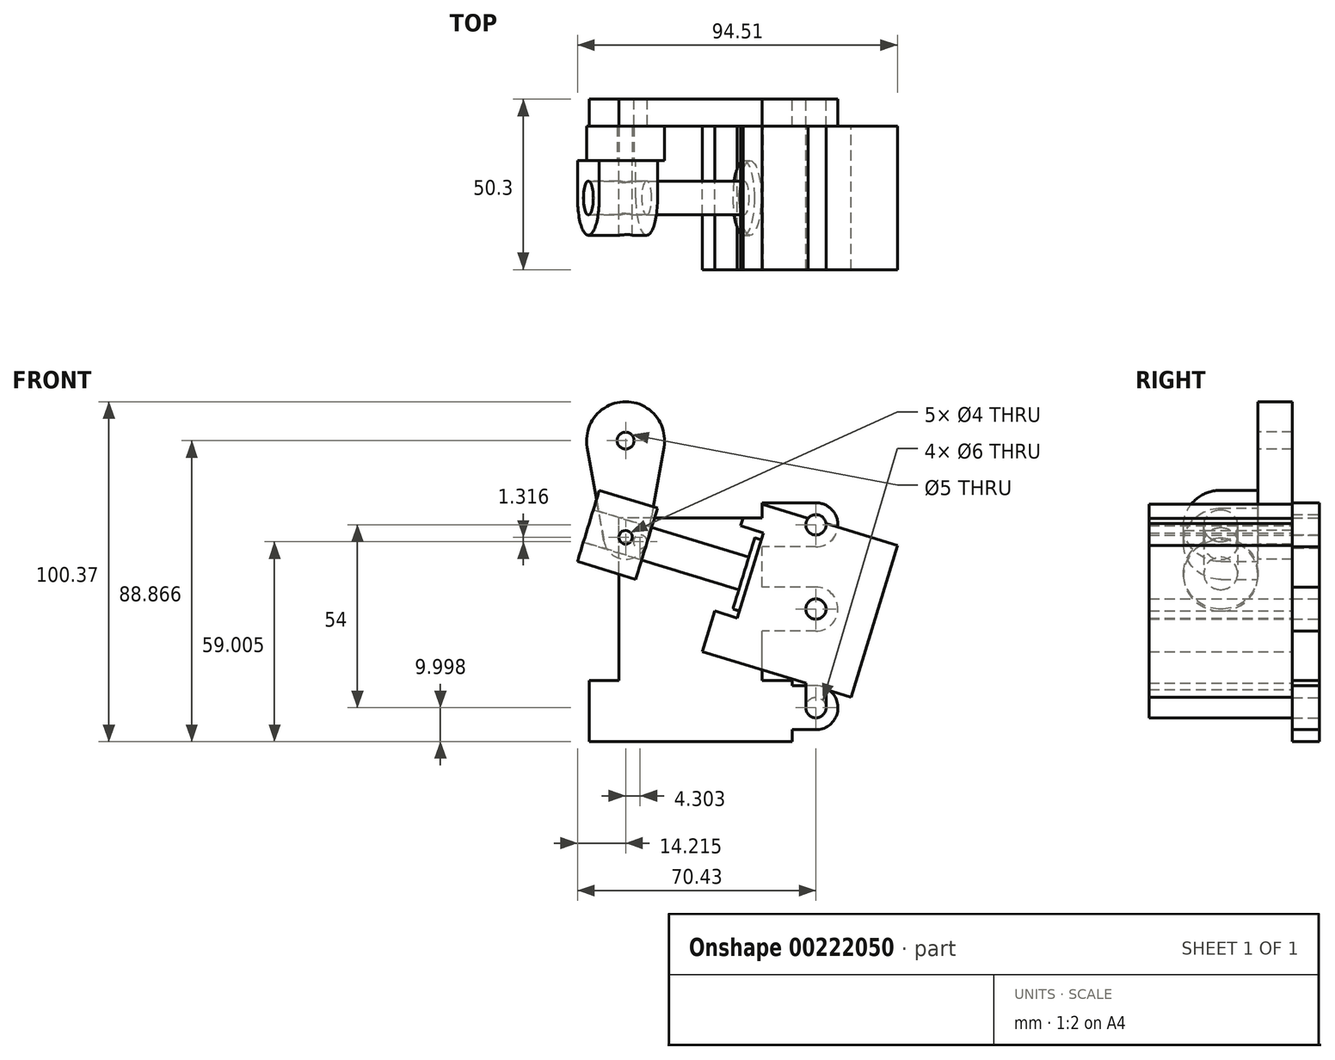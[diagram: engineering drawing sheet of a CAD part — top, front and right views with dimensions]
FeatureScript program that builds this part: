
annotation { "Feature Type Name" : "Feature", "Feature Type Description" : "" }
export const myFeature = defineFeature(function(context is Context, id is Id, definition is map)
    precondition{}
    {
        {
            var Q0;
            Q0=qCreatedBy(makeId("Front.planeOp"),FACE);
            var sketch = newSketch(context, id + "F0", { "sketchPlane" : qUnion([Q0])});
            skLineSegment(sketch, "E0.bottom", {"start": v(21.15, 20.37) * mm, "end": v(-21.15, 20.37) * mm});
            skLineSegment(sketch, "E0.top", {"start": v(21.15, 68.37) * mm, "end": v(-21.15, 68.37) * mm});
            skLineSegment(sketch, "E0.left", {"start": v(21.15, 20.37) * mm, "end": v(21.15, 68.37) * mm});
            skLineSegment(sketch, "E0.right", {"start": v(-21.15, 20.37) * mm, "end": v(-21.15, 68.37) * mm});
            skPoint(sketch, "E0.middle", {"position": v(0, 44.37) * mm});
            skLineSegment(sketch, "E1.bottom", {"start": v(-21.15, 68.37) * mm, "end": v(21.15, 68.37) * mm});
            skLineSegment(sketch, "E1.top", {"start": v(-21.15, 73.37) * mm, "end": v(21.15, 73.37) * mm});
            skLineSegment(sketch, "E1.left", {"start": v(-21.15, 68.37) * mm, "end": v(-21.15, 73.37) * mm});
            skLineSegment(sketch, "E1.right", {"start": v(21.15, 68.37) * mm, "end": v(21.15, 73.37) * mm});
            skLineSegment(sketch, "E2.bottom", {"start": v(30, 20.37) * mm, "end": v(-30, 20.37) * mm});
            skLineSegment(sketch, "E2.top", {"start": v(30, 2.37) * mm, "end": v(-30, 2.37) * mm});
            skLineSegment(sketch, "E2.left", {"start": v(30, 20.37) * mm, "end": v(30, 2.37) * mm});
            skLineSegment(sketch, "E2.right", {"start": v(-30, 20.37) * mm, "end": v(-30, 2.37) * mm});
            skPoint(sketch, "E2.middle", {"position": v(0, 11.37) * mm});
            skPoint(sketch, "E2.middle.positionSnap0", {"position": v(0, 20.37) * mm});
            skPoint(sketch, "E2.cornerSnap0", {"position": v(0, 20.37) * mm});
            skPoint(sketch, "E2.centerSnap0", {"position": v(0, 20.37) * mm});
            skCircle(sketch, "E3", {"center": v(37, 12.37) * mm, "radius": 6.5 * mm});
            skLineSegment(sketch, "E4", {"start": v(37, 5.87) * mm, "end": v(30, 5.87) * mm});
            skLineSegment(sketch, "E5", {"start": v(37, 18.87) * mm, "end": v(30, 18.87) * mm});
            skCircle(sketch, "E6", {"center": v(37, 12.37) * mm, "radius": 3 * mm});
            skCircle(sketch, "E7", {"center": v(37, 66.37) * mm, "radius": 6.5 * mm});
            skCircle(sketch, "E8", {"center": v(37, 66.37) * mm, "radius": 3 * mm});
            skLineSegment(sketch, "E9", {"start": v(37, 72.87) * mm, "end": v(21.15, 72.87) * mm});
            skLineSegment(sketch, "E10", {"start": v(37, 59.87) * mm, "end": v(21.15, 59.87) * mm});
            skCircle(sketch, "E11", {"center": v(37, 41.5) * mm, "radius": 6.5 * mm});
            skCircle(sketch, "E12", {"center": v(37, 41.5) * mm, "radius": 3 * mm});
            skLineSegment(sketch, "E13", {"start": v(37, 48) * mm, "end": v(21.15, 48) * mm});
            skLineSegment(sketch, "E14", {"start": v(37, 35) * mm, "end": v(21.15, 35) * mm});
            skSolve(sketch);
        }
        {
            var Q0;
            Q0=makeQuery(id+"F0.imprint","IMPRINT",FACE,{"disambiguationData":[TD([[makeQuery(id+"F0.imprint","IMPRINT",EDGE,{"derivedFrom":sQuery(id+"F0.wireOp",EDGE,"E1.bottom")}),1.0]])]});
            var Q1;
            {var subQ0=sQuery(id+"F0.wireOp",EDGE,"E0.left");Q1=makeQuery(id+"F0.imprint","IMPRINT",FACE,{"disambiguationData":[TD([[makeQuery(id+"F0.imprint","IMPRINT",EDGE,{"derivedFrom":subQ0}),1.0]])]});}
            var Q2;
            {var subQ0=sQuery(id+"F0.wireOp",EDGE,"E2.top");Q2=makeQuery(id+"F0.imprint","IMPRINT",FACE,{"disambiguationData":[TD([[makeQuery(id+"F0.imprint","IMPRINT",EDGE,{"derivedFrom":subQ0}),-1.0]])]});}
            var Q3;
            {var subQ0=sQuery(id+"F0.wireOp",EDGE,"E4");Q3=makeQuery(id+"F0.imprint","IMPRINT",FACE,{"disambiguationData":[TD([[makeQuery(id+"F0.imprint","IMPRINT",EDGE,{"derivedFrom":subQ0}),-1.0]])]});}
            var Q4;
            Q4=makeQuery(id+"F0.imprint","IMPRINT",FACE,{"disambiguationData":[TD([[makeQuery(id+"F0.imprint","IMPRINT",EDGE,{"derivedFrom":sQuery(id+"F0.wireOp",EDGE,"E6")}),-1.0]])]});
            var Q5;
            {var subQ0=sQuery(id+"F0.wireOp",EDGE,"E9");Q5=makeQuery(id+"F0.imprint","IMPRINT",FACE,{"disambiguationData":[TD([[makeQuery(id+"F0.imprint","IMPRINT",EDGE,{"derivedFrom":subQ0}),1.0]])]});}
            var Q6;
            Q6=makeQuery(id+"F0.imprint","IMPRINT",FACE,{"disambiguationData":[TD([[makeQuery(id+"F0.imprint","IMPRINT",EDGE,{"derivedFrom":sQuery(id+"F0.wireOp",EDGE,"E8")}),-1.0]])]});
            var Q7;
            Q7=makeQuery(id+"F0.imprint","IMPRINT",FACE,{"disambiguationData":[TD([[makeQuery(id+"F0.imprint","IMPRINT",EDGE,{"derivedFrom":sQuery(id+"F0.wireOp",EDGE,"E12")}),-1.0]])]});
            var Q8;
            {var subQ0=sQuery(id+"F0.wireOp",EDGE,"E13");Q8=makeQuery(id+"F0.imprint","IMPRINT",FACE,{"disambiguationData":[TD([[makeQuery(id+"F0.imprint","IMPRINT",EDGE,{"derivedFrom":subQ0}),1.0]])]});}
            extrude(context, id + "F1", {"entities" : qUnion([Q0, Q1, Q2, Q3, Q4, Q5, Q6, Q7, Q8]), "depth" : 8 * mm, "offsetDistance" : 25 * mm});
        }
        {
            var Q0;
            Q0=makeQuery(id+"F1.opExtrude","CAP_FACE",FACE,{"disambiguationData":[OSD([sQuery(id+"F0.wireOp",EDGE,"E0.left"),sQuery(id+"F0.wireOp",EDGE,"E0.right"),sQuery(id+"F0.wireOp",EDGE,"E1.top"),sQuery(id+"F0.wireOp",EDGE,"E1.left"),sQuery(id+"F0.wireOp",EDGE,"E1.right"),sQuery(id+"F0.wireOp",EDGE,"E2.bottom"),sQuery(id+"F0.wireOp",EDGE,"E2.top"),sQuery(id+"F0.wireOp",EDGE,"E2.left"),sQuery(id+"F0.wireOp",EDGE,"E2.right"),sQuery(id+"F0.wireOp",EDGE,"E3"),sQuery(id+"F0.wireOp",EDGE,"E4"),sQuery(id+"F0.wireOp",EDGE,"E5"),sQuery(id+"F0.wireOp",EDGE,"E6")])],"isStart":false});
            var sketch = newSketch(context, id + "F2", { "sketchPlane" : qUnion([Q0])});
            skCircle(sketch, "E15.0", {"center": v(37, 12.37) * mm, "radius": 3 * mm});
            skLineSegment(sketch, "E16", {"start": v(23.79, 71.66) * mm, "end": v(11.42, 31.2) * mm});
            skLineSegment(sketch, "E17", {"start": v(11.42, 31.2) * mm, "end": v(43.93, 21.27) * mm});
            skLineSegment(sketch, "E18", {"start": v(43.93, 21.27) * mm, "end": v(56.3, 61.72) * mm});
            skLineSegment(sketch, "E19", {"start": v(56.3, 61.72) * mm, "end": v(23.79, 71.66) * mm});
            skLineSegment(sketch, "E20", {"start": v(23.79, 71.66) * mm, "end": v(17.1, 73.7) * mm});
            skLineSegment(sketch, "E21", {"start": v(17.1, 73.7) * mm, "end": v(14.75, 66.06) * mm});
            skLineSegment(sketch, "E22", {"start": v(14.75, 66.06) * mm, "end": v(21.45, 64) * mm});
            skLineSegment(sketch, "E23", {"start": v(11.42, 31.2) * mm, "end": v(4.73, 33.25) * mm});
            skLineSegment(sketch, "E24", {"start": v(4.73, 33.25) * mm, "end": v(7.06, 40.9) * mm});
            skLineSegment(sketch, "E25", {"start": v(7.06, 40.9) * mm, "end": v(13.76, 38.86) * mm});
            skLineSegment(sketch, "E26", {"start": v(4.73, 33.25) * mm, "end": v(3.4, 28.95) * mm});
            skLineSegment(sketch, "E27", {"start": v(43.93, 21.27) * mm, "end": v(42.62, 16.96) * mm});
            skLineSegment(sketch, "E28", {"start": v(3.4, 28.95) * mm, "end": v(42.62, 16.96) * mm});
            skLineSegment(sketch, "E29", {"start": v(56.3, 61.72) * mm, "end": v(61.08, 60.26) * mm});
            skLineSegment(sketch, "E30", {"start": v(61.08, 60.26) * mm, "end": v(47.4, 15.5) * mm});
            skLineSegment(sketch, "E31", {"start": v(42.62, 16.96) * mm, "end": v(47.4, 15.5) * mm});
            skCircle(sketch, "E32.0", {"center": v(37, 66.37) * mm, "radius": 3 * mm});
            skCircle(sketch, "E33.0", {"center": v(37, 41.5) * mm, "radius": 3 * mm});
            skLineSegment(sketch, "E34", {"start": v(34, 12.37) * mm, "end": v(34, 19.6) * mm});
            skLineSegment(sketch, "E35", {"start": v(40, 12.37) * mm, "end": v(40, 17.76) * mm});
            skSolve(sketch);
        }
        {
            var Q0;
            {var subQ1=sQuery(id+"F2.wireOp",EDGE,"E18");Q0=makeQuery(id+"F2.imprint","IMPRINT",FACE,{"disambiguationData":[TD([[makeQuery(id+"F2.imprint","IMPRINT",EDGE,{"derivedFrom":subQ1}),1.0]])]});}
            var Q1;
            Q1=makeQuery(id+"F2.imprint","IMPRINT",FACE,{"disambiguationData":[TD([[makeQuery(id+"F2.imprint","IMPRINT",EDGE,{"derivedFrom":sQuery(id+"F2.wireOp",EDGE,"E33.0")}),-1.0]])]});
            var Q2;
            {var subQ0=sQuery(id+"F2.wireOp",EDGE,"E22");Q2=makeQuery(id+"F2.imprint","IMPRINT",FACE,{"disambiguationData":[TD([[makeQuery(id+"F2.imprint","IMPRINT",EDGE,{"derivedFrom":subQ0}),1.0]])]});}
            var Q3;
            {var subQ0=sQuery(id+"F2.wireOp",EDGE,"E23");Q3=makeQuery(id+"F2.imprint","IMPRINT",FACE,{"disambiguationData":[TD([[makeQuery(id+"F2.imprint","IMPRINT",EDGE,{"derivedFrom":subQ0}),-1.0]])]});}
            var Q4;
            {var subQ5=sQuery(id+"F2.wireOp",EDGE,"E23");Q4=makeQuery(id+"F2.imprint","IMPRINT",FACE,{"disambiguationData":[TD([[makeQuery(id+"F2.imprint","IMPRINT",EDGE,{"derivedFrom":subQ5}),1.0]])]});}
            var Q5;
            {var subQ7=sQuery(id+"F2.wireOp",EDGE,"E27");Q5=makeQuery(id+"F2.imprint","IMPRINT",FACE,{"disambiguationData":[TD([[makeQuery(id+"F2.imprint","IMPRINT",EDGE,{"derivedFrom":subQ7}),-1.0]])]});}
            var Q6;
            {var subQ0=sQuery(id+"F2.wireOp",EDGE,"E15.0");var subQ1=makeQuery(id+"F2.imprint","INTERSECT",VERTEX,{"derivedFrom":[subQ0,sQuery(id+"F2.wireOp",EDGE,"E34")]});Q6=makeQuery(id+"F2.imprint","IMPRINT",FACE,{"disambiguationData":[TD([[makeQuery(id+"F2.imprint","IMPRINT",EDGE,{"disambiguationData":[TD([[subQ1,1.0]])],"derivedFrom":subQ0}),1.0]])]});}
            var Q7;
            {var subQ0=sQuery(id+"F2.wireOp",EDGE,"E35");Q7=makeQuery(id+"F2.imprint","IMPRINT",FACE,{"disambiguationData":[TD([[makeQuery(id+"F2.imprint","IMPRINT",EDGE,{"derivedFrom":subQ0}),1.0]])]});}
            var Q8;
            {var subQ0=sQuery(id+"F2.wireOp",EDGE,"E28");var subQ1=makeQuery(id+"F2.imprint","INTERSECT",VERTEX,{"derivedFrom":[subQ0,sQuery(id+"F2.wireOp",EDGE,"E35")]});Q8=makeQuery(id+"F2.imprint","IMPRINT",FACE,{"disambiguationData":[TD([[makeQuery(id+"F2.imprint","IMPRINT",EDGE,{"disambiguationData":[TD([[subQ1,1.0]])],"derivedFrom":subQ0}),1.0]])]});}
            var Q9;
            {var subQ0=sQuery(id+"F2.wireOp",EDGE,"E34");var subQ1=sQuery(id+"F2.wireOp",EDGE,"E28");var subQ2=makeQuery(id+"F2.imprint","INTERSECT",VERTEX,{"derivedFrom":[subQ1,subQ0]});Q9=makeQuery(id+"F2.imprint","IMPRINT",FACE,{"disambiguationData":[TD([[makeQuery(id+"F2.imprint","IMPRINT",EDGE,{"disambiguationData":[TD([[subQ2,-1.0]])],"derivedFrom":subQ1}),-1.0]])]});}
            var Q10;
            Q10=makeQuery(id+"F2.imprint","IMPRINT",FACE,{"disambiguationData":[TD([[makeQuery(id+"F2.imprint","IMPRINT",EDGE,{"derivedFrom":sQuery(id+"F2.wireOp",EDGE,"E18")}),-1.0]])]});
            extrude(context, id + "F3", {"entities" : qUnion([Q0, Q1, Q2, Q3, Q4, Q5, Q6, Q7, Q8, Q9, Q10]), "depth" : 42.3 * mm, "offsetDistance" : 25 * mm});
        }
        {
            var Q0;
            Q0=makeQuery(id+"F3.opExtrude","SWEPT_FACE",FACE,{"disambiguationData":[OSD([sQuery(id+"F2.wireOp",EDGE,"E16")])]});
            var sketch = newSketch(context, id + "F4", { "sketchPlane" : qUnion([Q0])});
            skCircle(sketch, "E36", {"center": v(29.15, 54.33) * mm, "radius": 5 * mm});
            skPoint(sketch, "E36.centerSnap0", {"position": v(29.15, 67.48) * mm});
            skPoint(sketch, "E36.centerSnap1", {"position": v(50.3, 54.33) * mm});
            skSolve(sketch);
        }
        {
            var Q0;
            Q0=makeQuery(id+"F4.imprint","IMPRINT",FACE,{"disambiguationData":[TD([[makeQuery(id+"F4.imprint","IMPRINT",EDGE,{"derivedFrom":sQuery(id+"F4.wireOp",EDGE,"E36")}),1.0]])]});
            extrude(context, id + "F5", {"entities" : qUnion([Q0]), "operationType" : NewBodyOperationType.ADD, "depth" : 50 * mm, "offsetDistance" : 25 * mm});
        }
        {
            var Q0;
            Q0=makeQuery(id+"F5.opExtrude","CAP_FACE",FACE,{"disambiguationData":[OSD([sQuery(id+"F4.wireOp",EDGE,"E36")])],"isStart":false});
            var sketch = newSketch(context, id + "F6", { "sketchPlane" : qUnion([Q0])});
            skCircle(sketch, "E37.0", {"center": v(29.15, 54.33) * mm, "radius": 5 * mm});
            skCircle(sketch, "E38", {"center": v(29.15, 54.33) * mm, "radius": 11 * mm});
            skLineSegment(sketch, "E39", {"start": v(29.15, 65.33) * mm, "end": v(18.15, 65.33) * mm});
            skLineSegment(sketch, "E40", {"start": v(29.15, 43.33) * mm, "end": v(18.15, 43.33) * mm});
            skLineSegment(sketch, "E41", {"start": v(18.15, 43.33) * mm, "end": v(18.15, 65.33) * mm});
            skSolve(sketch);
        }
        {
            var Q0;
            Q0=makeQuery(id+"F6.imprint","IMPRINT",FACE,{"disambiguationData":[TD([[makeQuery(id+"F6.imprint","IMPRINT",EDGE,{"derivedFrom":sQuery(id+"F6.wireOp",EDGE,"E37.0")}),-1.0]])]});
            var Q1;
            {var subQ0=sQuery(id+"F6.wireOp",EDGE,"E39");Q1=makeQuery(id+"F6.imprint","IMPRINT",FACE,{"disambiguationData":[TD([[makeQuery(id+"F6.imprint","IMPRINT",EDGE,{"derivedFrom":subQ0}),1.0]])]});}
            var Q2;
            {var subQ0=sQuery(id+"F6.wireOp",EDGE,"E40");Q2=makeQuery(id+"F6.imprint","IMPRINT",FACE,{"disambiguationData":[TD([[makeQuery(id+"F6.imprint","IMPRINT",EDGE,{"derivedFrom":subQ0}),-1.0]])]});}
            extrude(context, id + "F7", {"entities" : qUnion([Q0, Q1, Q2]), "oppositeDirection" : true, "depth" : 18 * mm, "offsetDistance" : 25 * mm});
        }
        {
            var Q0;
            Q0=makeQuery(id+"F3.opExtrude","SWEPT_FACE",FACE,{"disambiguationData":[OSD([sQuery(id+"F2.wireOp",EDGE,"E16")])]});
            var sketch = newSketch(context, id + "F8", { "sketchPlane" : qUnion([Q0])});
            skCircle(sketch, "E42.0", {"center": v(29.15, 54.33) * mm, "radius": 5 * mm});
            skCircle(sketch, "E43", {"center": v(29.15, 54.33) * mm, "radius": 11 * mm});
            skSolve(sketch);
        }
        {
            var Q0;
            Q0=makeQuery(id+"F8.imprint","IMPRINT",FACE,{"disambiguationData":[TD([[makeQuery(id+"F8.imprint","IMPRINT",EDGE,{"derivedFrom":sQuery(id+"F8.wireOp",EDGE,"E42.0")}),-1.0]])]});
            extrude(context, id + "F9", {"entities" : qUnion([Q0]), "operationType" : NewBodyOperationType.ADD, "depth" : 2 * mm, "offsetDistance" : 25 * mm});
        }
        {
            var Q0;
            Q0=makeQuery(id+"F7.opExtrude","SWEPT_FACE",FACE,{"disambiguationData":[OSD([sQuery(id+"F6.wireOp",EDGE,"E41")])]});
            var sketch = newSketch(context, id + "F10", { "sketchPlane" : qUnion([Q0])});
            skLineSegment(sketch, "E44", {"start": v(13, 60.79) * mm, "end": v(19.21, 62.7) * mm});
            skCircle(sketch, "E45", {"center": v(19.21, 62.7) * mm, "radius": 2 * mm});
            skSolve(sketch);
        }
        {
            var Q0;
            Q0=makeQuery(id+"F10.imprint","IMPRINT",FACE,{"disambiguationData":[TD([[makeQuery(id+"F10.imprint","IMPRINT",EDGE,{"derivedFrom":sQuery(id+"F10.wireOp",EDGE,"E45")}),1.0]])]});
            extrude(context, id + "F11", {"entities" : qUnion([Q0]), "operationType" : NewBodyOperationType.REMOVE, "oppositeDirection" : true, "depth" : 25 * mm, "offsetDistance" : 25 * mm});
        }
        {
            var Q0;
            Q0=makeQuery(id+"F7.opExtrude","SWEPT_FACE",FACE,{"disambiguationData":[OSD([sQuery(id+"F6.wireOp",EDGE,"E41")])]});
            var sketch = newSketch(context, id + "F12", { "sketchPlane" : qUnion([Q0])});
            skCircle(sketch, "E46.0", {"center": v(19.21, 62.7) * mm, "radius": 2 * mm});
            skCircle(sketch, "E47", {"center": v(19.21, 62.7) * mm, "radius": 6.5 * mm});
            skCircle(sketch, "E48", {"center": v(19.21, 91.24) * mm, "radius": 11.5 * mm});
            skLineSegment(sketch, "E49", {"start": v(31.39, 94) * mm, "end": v(25.57, 61.3) * mm});
            skLineSegment(sketch, "E50", {"start": v(6.65, 96.18) * mm, "end": v(13.44, 58.04) * mm});
            skCircle(sketch, "E51", {"center": v(19.21, 91.24) * mm, "radius": 2.5 * mm});
            skSolve(sketch);
        }
        {
            var Q0;
            Q0=makeQuery(id+"F12.imprint","IMPRINT",FACE,{"disambiguationData":[TD([[makeQuery(id+"F12.imprint","IMPRINT",EDGE,{"derivedFrom":sQuery(id+"F12.wireOp",EDGE,"E51")}),-1.0]])]});
            var Q1;
            {var subQ1=sQuery(id+"F12.wireOp",EDGE,"E48");var subQ6=sQuery(id+"F12.wireOp",EDGE,"E49");var subQ7=makeQuery(id+"F12.imprint","INTERSECT",VERTEX,{"derivedFrom":[subQ1,subQ6]});Q1=makeQuery(id+"F12.imprint","IMPRINT",FACE,{"disambiguationData":[TD([[makeQuery(id+"F12.imprint","IMPRINT",EDGE,{"disambiguationData":[TD([[subQ7,1.0]])],"derivedFrom":subQ1}),-1.0]])]});}
            var Q2;
            Q2=makeQuery(id+"F12.imprint","IMPRINT",FACE,{"disambiguationData":[TD([[makeQuery(id+"F12.imprint","IMPRINT",EDGE,{"derivedFrom":sQuery(id+"F12.wireOp",EDGE,"E46.0")}),-1.0]])]});
            var Q3;
            {var subQ6=sQuery(id+"F12.wireOp",EDGE,"E49");var subQ7=sQuery(id+"F12.wireOp",EDGE,"E47");var subQ8=makeQuery(id+"F12.imprint","INTERSECT",VERTEX,{"derivedFrom":[subQ7,subQ6]});Q3=makeQuery(id+"F12.imprint","IMPRINT",FACE,{"disambiguationData":[TD([[makeQuery(id+"F12.imprint","IMPRINT",EDGE,{"disambiguationData":[TD([[subQ8,-1.0]])],"derivedFrom":subQ7}),-1.0]])]});}
            var Q4;
            {var subQ0=sQuery(id+"F0.wireOp",EDGE,"E9");var subQ1=sQuery(id+"F0.wireOp",EDGE,"E2.bottom");var subQ2=sQuery(id+"F0.wireOp",EDGE,"E0.right");var subQ3=sQuery(id+"F0.wireOp",EDGE,"E2.right");var subQ4=sQuery(id+"F0.wireOp",EDGE,"E8");var subQ5=sQuery(id+"F0.wireOp",EDGE,"E0.left");var subQ7=sQuery(id+"F0.wireOp",EDGE,"E2.left");var subQ8=sQuery(id+"F0.wireOp",EDGE,"E7");var subQ9=sQuery(id+"F0.wireOp",EDGE,"E1.right");var subQ10=sQuery(id+"F0.wireOp",EDGE,"E14");var subQ11=sQuery(id+"F0.wireOp",EDGE,"E13");var subQ12=sQuery(id+"F0.wireOp",EDGE,"E1.top");var subQ13=sQuery(id+"F0.wireOp",EDGE,"E10");var subQ14=sQuery(id+"F0.wireOp",EDGE,"E1.left");var subQ15=sQuery(id+"F0.wireOp",EDGE,"E11");var subQ16=sQuery(id+"F0.wireOp",EDGE,"E12");Q4=makeQuery(id+"FkcwUZqjYWmgQli_3.boolean.opBoolean","SPLIT",FACE,{"disambiguationData":[TD([makeQuery(id+"F1.opExtrude","SWEPT_FACE",FACE,{"disambiguationData":[OSD([subQ12])]})])],"derivedFrom":makeQuery(id+"F1.opExtrude","CAP_FACE",FACE,{"disambiguationData":[OSD([subQ5,subQ2,subQ12,subQ14,subQ9,subQ1,sQuery(id+"F0.wireOp",EDGE,"E2.top"),subQ7,subQ3,sQuery(id+"F0.wireOp",EDGE,"E3"),sQuery(id+"F0.wireOp",EDGE,"E4"),sQuery(id+"F0.wireOp",EDGE,"E5"),sQuery(id+"F0.wireOp",EDGE,"E6"),subQ8,subQ4,subQ0,subQ13,subQ15,subQ16,subQ11,subQ10])],"isStart":false})});}
            extrude(context, id + "F13", {"entities" : qUnion([Q0, Q1, Q2, Q3]), "endBound" : BoundingType.UP_TO_SURFACE, "depth" : 25 * mm, "endBoundEntityFace" : qUnion([Q4]), "offsetDistance" : 25 * mm});
        }
        {
            var Q0;
            Q0=makeQuery(id+"F1.opExtrude","CAP_FACE",FACE,{"disambiguationData":[OSD([sQuery(id+"F0.wireOp",EDGE,"E0.left"),sQuery(id+"F0.wireOp",EDGE,"E0.right"),sQuery(id+"F0.wireOp",EDGE,"E1.top"),sQuery(id+"F0.wireOp",EDGE,"E1.left"),sQuery(id+"F0.wireOp",EDGE,"E1.right"),sQuery(id+"F0.wireOp",EDGE,"E2.bottom"),sQuery(id+"F0.wireOp",EDGE,"E2.top"),sQuery(id+"F0.wireOp",EDGE,"E2.left"),sQuery(id+"F0.wireOp",EDGE,"E2.right"),sQuery(id+"F0.wireOp",EDGE,"E3"),sQuery(id+"F0.wireOp",EDGE,"E4"),sQuery(id+"F0.wireOp",EDGE,"E5"),sQuery(id+"F0.wireOp",EDGE,"E6"),sQuery(id+"F0.wireOp",EDGE,"E7"),sQuery(id+"F0.wireOp",EDGE,"E8"),sQuery(id+"F0.wireOp",EDGE,"E9"),sQuery(id+"F0.wireOp",EDGE,"E10"),sQuery(id+"F0.wireOp",EDGE,"E11"),sQuery(id+"F0.wireOp",EDGE,"E12"),sQuery(id+"F0.wireOp",EDGE,"E13"),sQuery(id+"F0.wireOp",EDGE,"E14")])],"isStart":false});
            var sketch = newSketch(context, id + "F14", { "sketchPlane" : qUnion([Q0])});
            skLineSegment(sketch, "E52.0", {"start": v(12.47, 41.5) * mm, "end": v(18.9, 62.54) * mm});
            skLineSegment(sketch, "E53", {"start": v(15.7, 52.02) * mm, "end": v(-14.91, 61.37) * mm, "construction": true});
            skCircle(sketch, "E54", {"center": v(-14.91, 61.37) * mm, "radius": 2 * mm});
            skSolve(sketch);
        }
        {
            var Q0;
            Q0=makeQuery(id+"F14.imprint","IMPRINT",FACE,{"disambiguationData":[TD([[makeQuery(id+"F14.imprint","IMPRINT",EDGE,{"derivedFrom":sQuery(id+"F14.wireOp",EDGE,"E54")}),1.0]])]});
            var Q1;
            Q1=sQuery(id+"F14.wireOp",EDGE,"E53");
            var Q2;
            Q2=sQuery(id+"F14.wireOp",EDGE,"E54");
            extrude(context, id + "F15", {"entities" : qUnion([Q0]), "operationType" : NewBodyOperationType.REMOVE, "surfaceEntities" : qUnion([Q1, Q2]), "oppositeDirection" : true, "depth" : 25 * mm, "offsetDistance" : 25 * mm});
        }
    });
